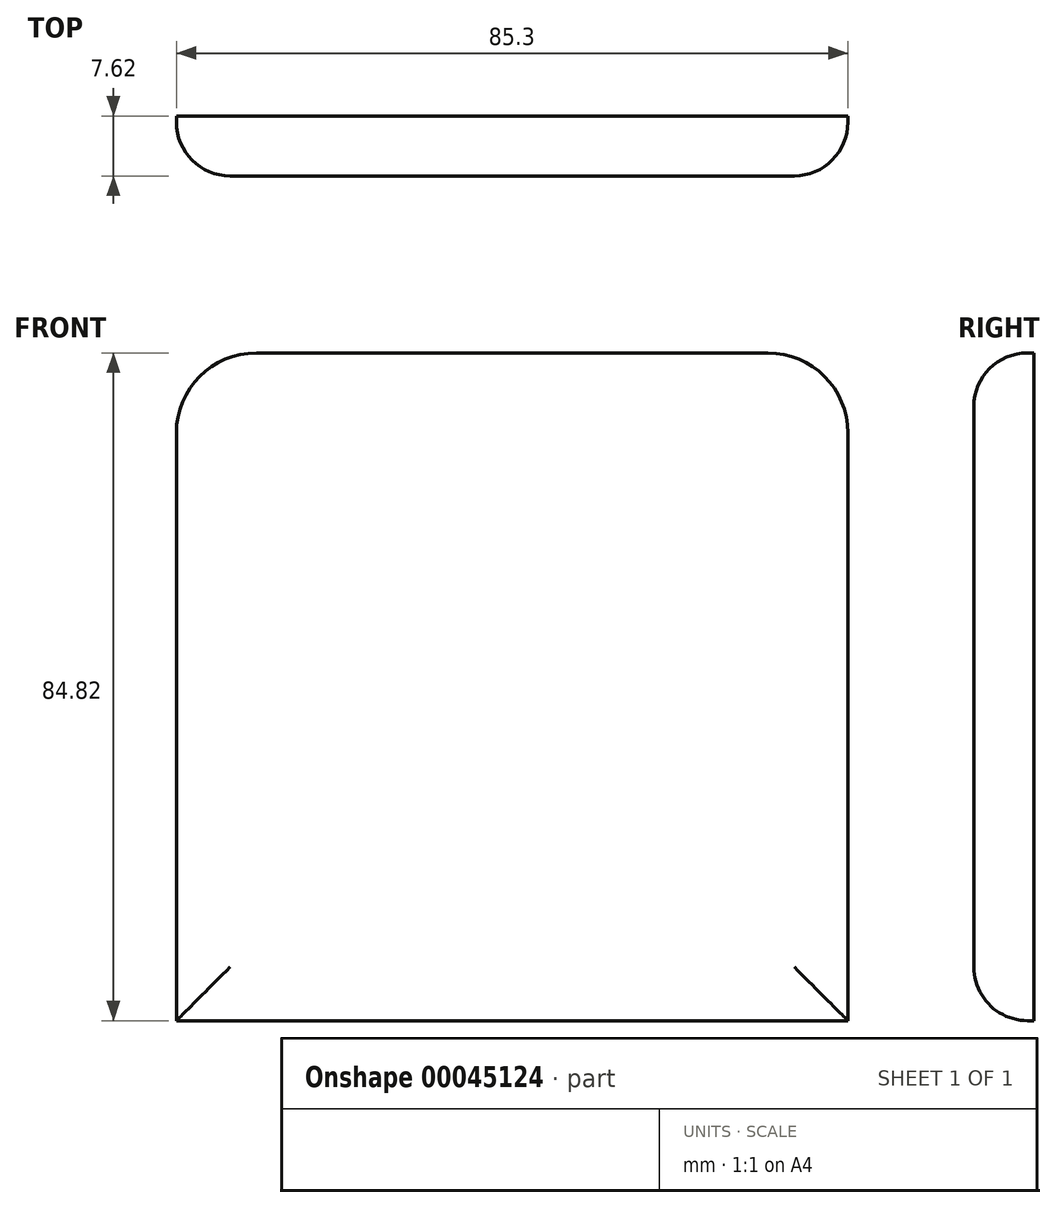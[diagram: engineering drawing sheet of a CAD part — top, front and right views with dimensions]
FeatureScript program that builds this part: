
annotation { "Feature Type Name" : "Feature", "Feature Type Description" : "" }
export const myFeature = defineFeature(function(context is Context, id is Id, definition is map)
    precondition{}
    {
        {
            var Q0;
            Q0=qCreatedBy(makeId("Front.planeOp"),FACE);
            var sketch = newSketch(context, id + "F0", { "sketchPlane" : qUnion([Q0])});
            skLineSegment(sketch, "E0.rect.bottom", {"start": v(38.1, 38.1) * mm, "end": v(-38.1, 38.1) * mm});
            skLineSegment(sketch, "E0.rect.top", {"start": v(38.1, -38.1) * mm, "end": v(-38.1, -38.1) * mm});
            skLineSegment(sketch, "E0.rect.left", {"start": v(38.1, 38.1) * mm, "end": v(38.1, -38.1) * mm});
            skLineSegment(sketch, "E0.rect.right", {"start": v(-38.1, 38.1) * mm, "end": v(-38.1, -38.1) * mm});
            skPoint(sketch, "E0.rect.middle", {"position": v(0, 0) * mm});
            skLineSegment(sketch, "E1", {"start": v(0, 38.1) * mm, "end": v(0, 25.4) * mm});
            skPoint(sketch, "E1.endSnap0", {"position": v(0, 38.1) * mm});
            skLineSegment(sketch, "E2", {"start": v(0, -38.1) * mm, "end": v(0, -25.4) * mm});
            skPoint(sketch, "E2.endSnap0", {"position": v(0, -38.1) * mm});
            skLineSegment(sketch, "E3.rect.bottom", {"start": v(25.4, 25.4) * mm, "end": v(-25.4, 25.4) * mm});
            skLineSegment(sketch, "E3.rect.top", {"start": v(25.4, -25.4) * mm, "end": v(-25.4, -25.4) * mm});
            skLineSegment(sketch, "E3.rect.left", {"start": v(25.4, 25.4) * mm, "end": v(25.4, -25.4) * mm});
            skLineSegment(sketch, "E3.rect.right", {"start": v(-25.4, 25.4) * mm, "end": v(-25.4, -25.4) * mm});
            skCircle(sketch, "E4", {"center": v(19.81, 12.95) * mm, "radius": 0.85 * mm});
            skCircle(sketch, "E5", {"center": v(-18.29, 12.95) * mm, "radius": 0.85 * mm});
            skCircle(sketch, "E6", {"center": v(-18.29, -12.45) * mm, "radius": 0.85 * mm});
            skCircle(sketch, "E7", {"center": v(19.81, -12.45) * mm, "radius": 0.85 * mm});
            skCircle(sketch, "E8", {"center": v(-18.29, 12.95) * mm, "radius": 1.9 * mm});
            skCircle(sketch, "E9", {"center": v(-18.29, -12.45) * mm, "radius": 1.9 * mm});
            skCircle(sketch, "E10", {"center": v(19.81, -12.45) * mm, "radius": 1.9 * mm});
            skCircle(sketch, "E11", {"center": v(19.81, 12.95) * mm, "radius": 1.9 * mm});
            skLineSegment(sketch, "E12.rect.bottom", {"start": v(42.65, 42.41) * mm, "end": v(-42.65, 42.41) * mm});
            skLineSegment(sketch, "E12.rect.top", {"start": v(42.65, -42.41) * mm, "end": v(-42.65, -42.41) * mm});
            skLineSegment(sketch, "E12.rect.left", {"start": v(42.65, 42.41) * mm, "end": v(42.65, -42.41) * mm});
            skLineSegment(sketch, "E12.rect.right", {"start": v(-42.65, 42.41) * mm, "end": v(-42.65, -42.41) * mm});
            skSolve(sketch);
        }
        {
            var Q0;
            {var subQ1=sQuery(id+"F0.wireOp",EDGE,"E0.rect.left");Q0=makeQuery(id+"F0.imprint","IMPRINT",FACE,{"disambiguationData":[TD([[makeQuery(id+"F0.imprint","IMPRINT",EDGE,{"derivedFrom":subQ1}),1.0]])]});}
            var Q1;
            {var subQ6=sQuery(id+"F0.wireOp",EDGE,"E0.rect.right");Q1=makeQuery(id+"F0.imprint","IMPRINT",FACE,{"disambiguationData":[TD([[makeQuery(id+"F0.imprint","IMPRINT",EDGE,{"derivedFrom":subQ6}),1.0]])]});}
            var Q2;
            Q2=makeQuery(id+"F0.imprint","IMPRINT",FACE,{"disambiguationData":[TD([[makeQuery(id+"F0.imprint","IMPRINT",EDGE,{"derivedFrom":sQuery(id+"F0.wireOp",EDGE,"E6")}),-1.0]])]});
            var Q3;
            Q3=makeQuery(id+"F0.imprint","IMPRINT",FACE,{"disambiguationData":[TD([[makeQuery(id+"F0.imprint","IMPRINT",EDGE,{"derivedFrom":sQuery(id+"F0.wireOp",EDGE,"E5")}),1.0]])]});
            var Q4;
            Q4=makeQuery(id+"F0.imprint","IMPRINT",FACE,{"disambiguationData":[TD([[makeQuery(id+"F0.imprint","IMPRINT",EDGE,{"derivedFrom":sQuery(id+"F0.wireOp",EDGE,"E5")}),-1.0]])]});
            var Q5;
            Q5=makeQuery(id+"F0.imprint","IMPRINT",FACE,{"disambiguationData":[TD([[makeQuery(id+"F0.imprint","IMPRINT",EDGE,{"derivedFrom":sQuery(id+"F0.wireOp",EDGE,"E4")}),-1.0]])]});
            var Q6;
            {var subQ6=sQuery(id+"F0.wireOp",EDGE,"E0.rect.left");Q6=makeQuery(id+"F0.imprint","IMPRINT",FACE,{"disambiguationData":[TD([[makeQuery(id+"F0.imprint","IMPRINT",EDGE,{"derivedFrom":subQ6}),-1.0]])]});}
            var Q7;
            Q7=makeQuery(id+"F0.imprint","IMPRINT",FACE,{"disambiguationData":[TD([[makeQuery(id+"F0.imprint","IMPRINT",EDGE,{"derivedFrom":sQuery(id+"F0.wireOp",EDGE,"E6")}),1.0]])]});
            var Q8;
            {var subQ1=sQuery(id+"F0.wireOp",EDGE,"E3.rect.left");Q8=makeQuery(id+"F0.imprint","IMPRINT",FACE,{"disambiguationData":[TD([[makeQuery(id+"F0.imprint","IMPRINT",EDGE,{"derivedFrom":subQ1}),-1.0]])]});}
            var Q9;
            Q9=makeQuery(id+"F0.imprint","IMPRINT",FACE,{"disambiguationData":[TD([[makeQuery(id+"F0.imprint","IMPRINT",EDGE,{"derivedFrom":sQuery(id+"F0.wireOp",EDGE,"E7")}),-1.0]])]});
            var Q10;
            Q10=makeQuery(id+"F0.imprint","IMPRINT",FACE,{"disambiguationData":[TD([[makeQuery(id+"F0.imprint","IMPRINT",EDGE,{"derivedFrom":sQuery(id+"F0.wireOp",EDGE,"E4")}),1.0]])]});
            var Q11;
            Q11=makeQuery(id+"F0.imprint","IMPRINT",FACE,{"disambiguationData":[TD([[makeQuery(id+"F0.imprint","IMPRINT",EDGE,{"derivedFrom":sQuery(id+"F0.wireOp",EDGE,"E7")}),1.0]])]});
            extrude(context, id + "F1", {"entities" : qUnion([Q0, Q1, Q2, Q3, Q4, Q5, Q6, Q7, Q8, Q9, Q10, Q11]), "depth" : 7.62 * mm});
        }
        {
            var Q0;
            Q0=makeQuery(id+"F1.opExtrude","CAP_EDGE",EDGE,{"disambiguationData":[OSD([sQuery(id+"F0.wireOp",EDGE,"E12.rect.top")])],"isStart":false});
            var Q1;
            Q1=makeQuery(id+"F1.opExtrude","CAP_EDGE",EDGE,{"disambiguationData":[OSD([sQuery(id+"F0.wireOp",EDGE,"E12.rect.right")])],"isStart":false});
            var Q2;
            Q2=makeQuery(id+"F1.opExtrude","CAP_EDGE",EDGE,{"disambiguationData":[OSD([sQuery(id+"F0.wireOp",EDGE,"E12.rect.bottom")])],"isStart":false});
            var Q3;
            Q3=makeQuery(id+"F1.opExtrude","CAP_EDGE",EDGE,{"disambiguationData":[OSD([sQuery(id+"F0.wireOp",EDGE,"E12.rect.left")])],"isStart":false});
            fillet(context, id + "F2", {"entities" : qUnion([Q0, Q1, Q2, Q3]), "radius" : 6.8 * mm, "tangentPropagation" : true, "allowEdgeOverflow" : false});
        }
        {
            var Q0;
            Q0=makeQuery(id+"F1.opExtrude","SWEPT_EDGE",EDGE,{"disambiguationData":[OSD([sQuery(id+"F0.wireOp",EDGE,"E12.rect.bottom"),sQuery(id+"F0.wireOp",EDGE,"E12.rect.left")])]});
            var Q1;
            Q1=makeQuery(id+"F1.opExtrude","SWEPT_EDGE",EDGE,{"disambiguationData":[OSD([sQuery(id+"F0.wireOp",EDGE,"E12.rect.bottom"),sQuery(id+"F0.wireOp",EDGE,"E12.rect.right")])]});
            fillet(context, id + "F3", {"entities" : qUnion([Q0, Q1]), "radius" : 10.16 * mm, "tangentPropagation" : true, "allowEdgeOverflow" : false});
        }
    });
